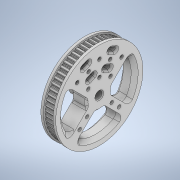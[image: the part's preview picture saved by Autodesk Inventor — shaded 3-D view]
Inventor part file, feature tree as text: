
AUTODESK INVENTOR PART (.ipt)
format: ipt  version: 2020 (Build 240168000, 168)  size: 2,600,448 bytes
history: native  units: mm
features: sketch x17, extrude x13, projected_geometry x13, thicken_offset x11, chamfer x6, hole x4, fillet x3, plane x2, other x1
ambient origin geometry x8: Origin, YZ Plane, XZ Plane, XY Plane, X Axis, Y Axis, Z Axis, Center Point
bodies: Solid1 (feature_tree)
feature tree (70):
  plane  "Work Plane1"
  extrude  "Extrusion1"  Depth=110.0mm
  plane  "Work Plane2"
  extrude  "Extrusion2"  [1 undecoded]
  extrude  "Extrusion3"  Depth=20.0mm TaperAngle=0.0deg
  thicken_offset  "Thicken1"
  extrude  "Extrusion4"  Depth=10.0mm
  extrude  "Extrusion5"  Depth=20.0mm TaperAngle=0.0deg
  extrude  "Extrusion6"  Depth=3.0mm TaperAngle=0.0deg
  extrude  "Extrusion7"  Depth=20.0mm
  extrude  "Extrusion8"  Depth=36.0mm
  hole  "Hole1"  [1 undecoded]
  hole  "Hole2"  [1 undecoded]
  hole  "Hole3"  [1 undecoded]
  extrude  "Extrusion9"  Depth=4.0mm
  thicken_offset  "Thicken2"
  thicken_offset  "Thicken3"
  thicken_offset  "Thicken4"
  extrude  "Extrusion10"  Depth=4.0mm
  thicken_offset  "Thicken5"
  thicken_offset  "Thicken6"
  extrude  "Extrusion11"  Depth=4.0mm
  extrude  "Extrusion12"  Depth=10.0mm
  chamfer  "Chamfer1"  Distance=4.0mm
  fillet  "Fillet1"  Radius=4.0mm
  chamfer  "Chamfer2"  Distance=85.0mm
  chamfer  "Chamfer5"  Distance=34.0mm
  chamfer  "Chamfer6"  Distance=42.5mm
  chamfer  "Chamfer4"  Distance=5.0mm
  extrude  "Extrusion13"  Depth=42.5mm
  chamfer  "Chamfer7"  Distance=5.0mm
  thicken_offset  "Thicken9"
  thicken_offset  "Thicken10"
  hole  "Hole4"  [1 undecoded]
  thicken_offset  "Thicken11"
  thicken_offset  "Thicken12"
  thicken_offset  "Thicken13"
  fillet  "Fillet5"  Radius=5.0mm
  fillet  "Fillet6"  Radius=5.0mm
  sketch  "Sketch1"  dims[d0=0.0mm d1=110.0mm]
  sketch  "Sketch2"  dims[d2=10.0mm d3=0.0mm d4=-1.0mm]
  sketch  "Sketch3"  dims[d5=110.0mm d6=20.0mm d7=0.0mm]
  projected_geometry  "Projected Loop1"
  sketch  "Sketch4"  dims[d8=20.0mm d9=0.0mm d10=10.0mm d11=9.0mm]
  projected_geometry  "Projected Loop2"
  sketch  "Sketch5"  dims[d12=8.15mm d13=20.0mm d14=0.0mm]
  sketch  "Sketch6"  dims[d15=102.0mm d16=3.0mm d17=0.0mm]
  sketch  "Sketch7"  dims[d18=3.0mm d19=0.0mm d20=20.0mm]
  projected_geometry  "Projected Loop3"
  sketch  "Sketch8"  dims[d21=8.0mm d22=0.0mm d23=36.0mm]
  projected_geometry  "Projected Loop4"
  sketch  "Sketch9"  dims[d24=4.0mm d25=36.0mm]
  projected_geometry  "Projected Loop5"
  sketch  "Sketch10"  dims[d26=45.0deg d27=45.0deg]
  projected_geometry  "Projected Loop6"
  sketch  "Sketch11"  dims[d28=36.0mm d29=45.0deg]
  projected_geometry  "Projected Loop7"
  sketch  "Sketch12"  dims[d30=4.0mm d31=4.0mm]
  projected_geometry  "Projected Loop8"
  sketch  "Sketch13"  dims[d32=20.0mm d33=0.0mm]
  projected_geometry  "Projected Loop9"
  sketch  "Sketch14"  dims[d34=4.15mm d35=6.0mm d36=4.0mm d37=2.0mm d38=90.0deg d39=20.0mm d40=0.0mm d41=4.0mm]
  projected_geometry  "Projected Loop10"
  sketch  "Sketch15"  dims[d42=4.0mm d43=4.0mm]
  projected_geometry  "Projected Loop11"
  sketch  "Sketch16"  dims[d44=4.15mm d45=6.0mm d46=4.0mm d47=2.0mm d48=90.0deg d49=20.0mm d50=0.0mm d51=10.0mm]
  projected_geometry  "Projected Loop12"
  sketch  "Sketch18"  dims[d52=10.0mm d53=4.0mm d54=4.0mm d55=4.15mm d56=6.0mm d57=4.0mm d58=2.0mm d59=90.0deg d60=20.0mm d61=0.0mm d62=85.0mm d63=34.0mm d64=42.5mm d65=5.0mm d66=42.5mm d67=5.0mm d68=5.0mm d69=5.0mm d70=5.0mm d71=5.0mm d72=2.85mm d73=20.0mm d74=0.0mm d75=2.0mm d76=2.0mm d77=2.0mm d78=2.0mm d79=2.0mm d80=2.0mm d81=81.0mm d82=20.0mm d83=0.0mm d84=2.0mm d85=2.0mm d86=2.0mm d87=2.0mm d88=8.0mm d89=3.0mm d90=4.0mm d91=8.0mm d92=3.0mm d93=4.0mm d94=20.0mm d95=0.0mm d96=8.0mm d97=8.0mm d98=3.0mm d99=4.0mm d100=3.0mm d101=4.0mm d102=20.0mm d103=0.0mm d104=4.0mm d105=2.0mm d106=45.0deg d107=5.0mm d108=4.0mm d109=2.0mm d110=45.0deg d116=2.0mm d117=2.0mm d118=45.0deg d119=3.0mm d120=2.0mm d121=45.0deg d122=1.0mm d123=2.0mm d124=45.0deg d125=20.0mm d126=20.0mm d127=4.0mm d128=4.0mm d129=20.0mm d130=0.0mm d136=2.0mm d137=2.0mm d138=45.0deg d143=1.0mm d144=1.0mm d145=1.0mm d146=1.0mm d147=12.0mm d148=12.0mm d149=4.15mm d150=6.0mm d151=4.0mm d152=2.0mm d153=90.0deg d154=20.0mm d155=0.0mm d156=2.0mm d157=2.0mm d158=2.0mm d159=2.0mm d160=2.0mm d161=2.0mm d162=3.0mm d163=3.0mm]
  projected_geometry  "Projected Loop14"
  other  "_ATP60XL037-A-C12_b"
note: 5 required parameter values undecoded (feature->parameter linkage not recoverable at this tier; creation-order binding heuristic only, values carry confidence <= 0.55)
